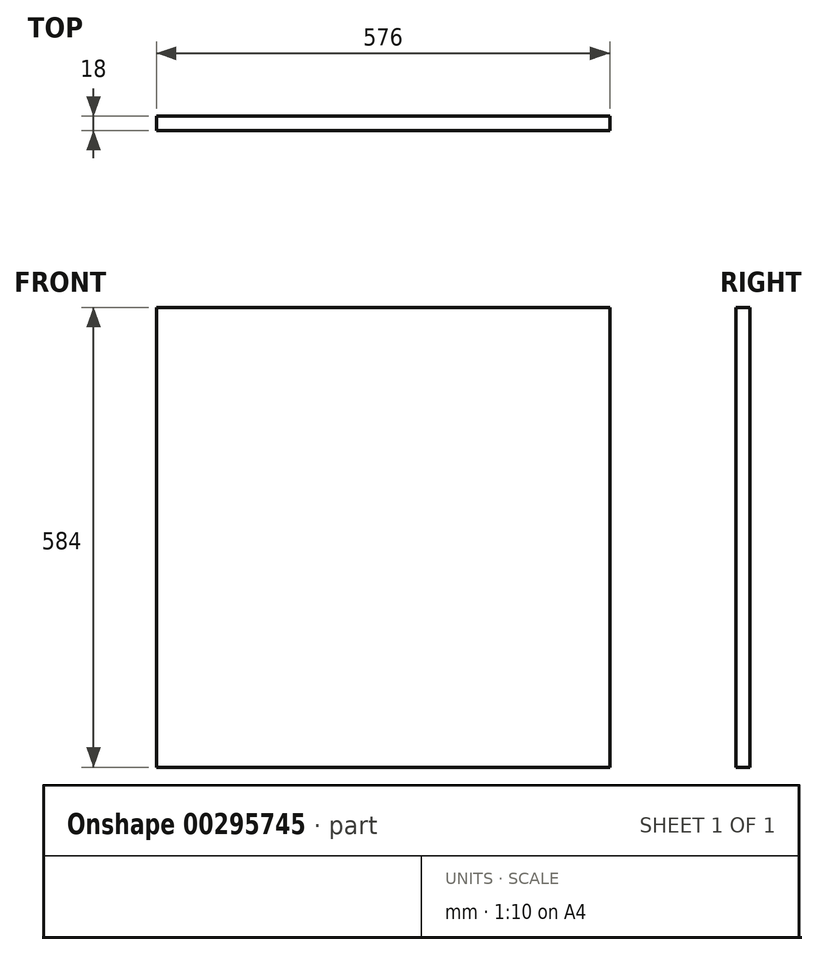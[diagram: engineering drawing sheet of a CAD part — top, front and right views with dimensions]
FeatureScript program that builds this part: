
annotation { "Feature Type Name" : "Feature", "Feature Type Description" : "" }
export const myFeature = defineFeature(function(context is Context, id is Id, definition is map)
    precondition{}
    {
        {
            var Q0;
            Q0=qCreatedBy(makeId("Front.planeOp"),FACE);
            var sketch = newSketch(context, id + "F0", { "sketchPlane" : qUnion([Q0])});
            skLineSegment(sketch, "E0.bottom", {"start": v(-292.6, 211.25) * mm, "end": v(283.4, 211.25) * mm});
            skLineSegment(sketch, "E0.top", {"start": v(-292.6, -372.75) * mm, "end": v(283.4, -372.75) * mm});
            skLineSegment(sketch, "E0.left", {"start": v(-292.6, 211.25) * mm, "end": v(-292.6, -372.75) * mm});
            skLineSegment(sketch, "E0.right", {"start": v(283.4, 211.25) * mm, "end": v(283.4, -372.75) * mm});
            skSolve(sketch);
        }
        {
            var Q0;
            Q0 = qSketchRegion(id + "F0", true);
            extrude(context, id + "F1", {"entities" : qUnion([Q0]), "depth" : 18 * mm});
        }
    });
